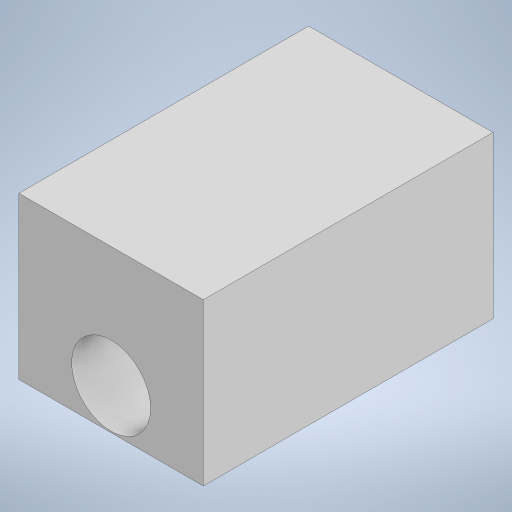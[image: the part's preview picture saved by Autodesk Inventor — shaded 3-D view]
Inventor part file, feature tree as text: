
AUTODESK INVENTOR PART (.ipt)
format: ipt  version: 2023 (Build 270158000, 158)  size: 177,664 bytes
history: native  units: mm
features: other x3, extrude x3, sketch x3, reference x1, projected_geometry x1
ambient origin geometry x8: Origin, YZ Plane, XZ Plane, XY Plane, X Axis, Y Axis, Z Axis, Center Point
bodies: Body1 (feature_tree)
feature tree (11):
  other  "Bryła1"
  extrude  "Wyciągnięcie proste1"  Depth=14.0mm
  extrude  "Wyciągnięcie proste2"  Depth=22.0mm
  extrude  "Wyciągnięcie proste3"  Depth=8.25mm TaperAngle=0.0deg
  sketch  "Szkic1"
  sketch  "Szkic2"
  reference  "Odniesienie1"
  sketch  "Szkic3"
  projected_geometry  "Pętla rzutowana1"
  other  "Zespół2"
  other  "silnik_2:1"
